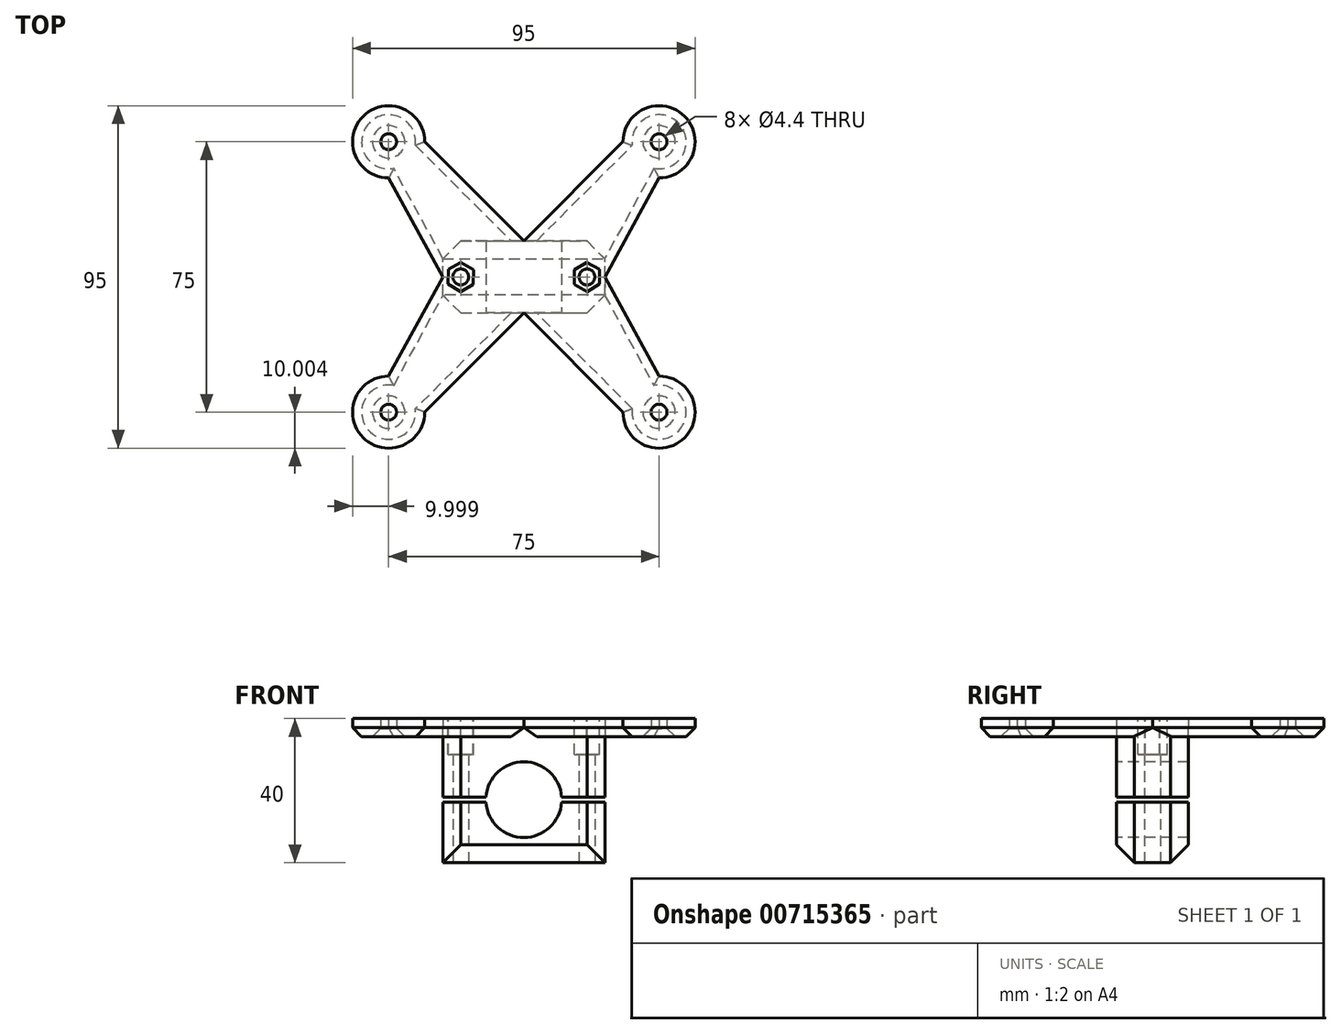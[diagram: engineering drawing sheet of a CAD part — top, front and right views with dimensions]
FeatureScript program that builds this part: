
annotation { "Feature Type Name" : "Feature", "Feature Type Description" : "" }
export const myFeature = defineFeature(function(context is Context, id is Id, definition is map)
    precondition{}
    {
        {
            var Q0;
            Q0=qCreatedBy(makeId("Top.planeOp"),FACE);
            var sketch = newSketch(context, id + "F0", { "sketchPlane" : qUnion([Q0])});
            skLineSegment(sketch, "E0.bottom", {"start": v(-29.97, 5.83) * mm, "end": v(15.03, 5.83) * mm});
            skLineSegment(sketch, "E0.top", {"start": v(-29.97, -14.17) * mm, "end": v(15.03, -14.17) * mm});
            skLineSegment(sketch, "E0.left", {"start": v(-29.97, 5.83) * mm, "end": v(-29.97, -14.17) * mm});
            skLineSegment(sketch, "E0.right", {"start": v(15.03, 5.83) * mm, "end": v(15.03, -14.17) * mm});
            skSolve(sketch);
        }
        {
            var Q0;
            Q0 = qSketchRegion(id + "F0", true);
            extrude(context, id + "F1", {"entities" : qUnion([Q0]), "depth" : 35 * mm, "offsetDistance" : 25 * mm});
        }
        {
            var Q0;
            Q0=makeQuery(id+"F1.opExtrude","SWEPT_FACE",FACE,{"disambiguationData":[OSD([sQuery(id+"F0.wireOp",EDGE,"E0.top")])]});
            var sketch = newSketch(context, id + "F2", { "sketchPlane" : qUnion([Q0])});
            skLineSegment(sketch, "E1", {"start": v(-7.47, 35) * mm, "end": v(-7.47, 0) * mm, "construction": true});
            skCircle(sketch, "E2", {"center": v(-7.47, 17.5) * mm, "radius": 10.5 * mm});
            skSolve(sketch);
        }
        {
            var Q0;
            Q0=makeQuery(id+"F2.imprint","IMPRINT",FACE,{"disambiguationData":[TD([[makeQuery(id+"F2.imprint","IMPRINT",EDGE,{"derivedFrom":sQuery(id+"F2.wireOp",EDGE,"E2")}),1.0]])]});
            extrude(context, id + "F3", {"entities" : qUnion([Q0]), "operationType" : NewBodyOperationType.REMOVE, "endBound" : BoundingType.UP_TO_NEXT, "oppositeDirection" : true, "depth" : 25 * mm, "offsetDistance" : 25 * mm});
        }
        {
            var Q0;
            Q0=makeQuery(id+"F1.opExtrude","CAP_FACE",FACE,{"disambiguationData":[OSD([sQuery(id+"F0.wireOp",EDGE,"E0.bottom"),sQuery(id+"F0.wireOp",EDGE,"E0.top"),sQuery(id+"F0.wireOp",EDGE,"E0.left"),sQuery(id+"F0.wireOp",EDGE,"E0.right")])],"isStart":false});
            var sketch = newSketch(context, id + "F4", { "sketchPlane" : qUnion([Q0])});
            skLineSegment(sketch, "E3", {"start": v(-7.47, 5.83) * mm, "end": v(-7.47, -14.17) * mm, "construction": true});
            skLineSegment(sketch, "E4.bottom", {"start": v(30.03, 33.33) * mm, "end": v(-44.97, 33.33) * mm});
            skLineSegment(sketch, "E4.top", {"start": v(30.03, -41.67) * mm, "end": v(-44.97, -41.67) * mm});
            skLineSegment(sketch, "E4.left", {"start": v(30.03, 33.33) * mm, "end": v(30.03, -41.67) * mm});
            skLineSegment(sketch, "E4.right", {"start": v(-44.97, 33.33) * mm, "end": v(-44.97, -41.67) * mm});
            skPoint(sketch, "E4.middle", {"position": v(-7.47, -4.17) * mm});
            skCircle(sketch, "E5", {"center": v(-44.97, 33.33) * mm, "radius": 10 * mm});
            skCircle(sketch, "E6", {"center": v(30.03, 33.33) * mm, "radius": 10 * mm});
            skCircle(sketch, "E7", {"center": v(30.03, -41.67) * mm, "radius": 10 * mm});
            skCircle(sketch, "E8", {"center": v(-44.97, -41.67) * mm, "radius": 10 * mm});
            skLineSegment(sketch, "E9", {"start": v(-44.97, -31.67) * mm, "end": v(-29.97, -4.17) * mm});
            skLineSegment(sketch, "E10", {"start": v(-34.97, -41.67) * mm, "end": v(-7.47, -14.17) * mm});
            skLineSegment(sketch, "E11", {"start": v(-7.47, -14.17) * mm, "end": v(20.03, -41.67) * mm});
            skLineSegment(sketch, "E12", {"start": v(-29.97, -4.17) * mm, "end": v(-44.97, 23.33) * mm});
            skLineSegment(sketch, "E13", {"start": v(-34.97, 33.33) * mm, "end": v(-7.47, 5.83) * mm});
            skLineSegment(sketch, "E14", {"start": v(-7.47, 5.83) * mm, "end": v(20.03, 33.33) * mm});
            skLineSegment(sketch, "E15", {"start": v(15.03, -4.17) * mm, "end": v(30.03, 23.33) * mm});
            skLineSegment(sketch, "E16", {"start": v(15.03, -4.17) * mm, "end": v(30.03, -31.67) * mm});
            skSolve(sketch);
        }
        {
            var Q0;
            {var subQ0=sQuery(id+"F4.wireOp",EDGE,"E4.right");var subQ1=sQuery(id+"F4.wireOp",EDGE,"E4.bottom");var subQ2=makeQuery(id+"F4.imprint","INTERSECT",VERTEX,{"derivedFrom":[subQ1,subQ0]});Q0=makeQuery(id+"F4.imprint","IMPRINT",FACE,{"disambiguationData":[TD([[makeQuery(id+"F4.imprint","IMPRINT",EDGE,{"disambiguationData":[TD([[subQ2,1.0]])],"derivedFrom":subQ1}),1.0]])]});}
            var Q1;
            {var subQ0=sQuery(id+"F4.wireOp",EDGE,"E4.right");var subQ1=sQuery(id+"F4.wireOp",EDGE,"E4.bottom");var subQ2=makeQuery(id+"F4.imprint","INTERSECT",VERTEX,{"derivedFrom":[subQ1,subQ0]});Q1=makeQuery(id+"F4.imprint","IMPRINT",FACE,{"disambiguationData":[TD([[makeQuery(id+"F4.imprint","IMPRINT",EDGE,{"disambiguationData":[TD([[subQ2,1.0]])],"derivedFrom":subQ1}),-1.0]])]});}
            var Q2;
            {var subQ1=sQuery(id+"F4.wireOp",EDGE,"E12");Q2=makeQuery(id+"F4.imprint","IMPRINT",FACE,{"disambiguationData":[TD([[makeQuery(id+"F4.imprint","IMPRINT",EDGE,{"derivedFrom":subQ1}),-1.0]])]});}
            var Q3;
            {var subQ4=sQuery(id+"F4.wireOp",EDGE,"E9");Q3=makeQuery(id+"F4.imprint","IMPRINT",FACE,{"disambiguationData":[TD([[makeQuery(id+"F4.imprint","IMPRINT",EDGE,{"derivedFrom":subQ4}),-1.0]])]});}
            var Q4;
            {var subQ0=sQuery(id+"F4.wireOp",EDGE,"E4.right");var subQ1=sQuery(id+"F4.wireOp",EDGE,"E4.top");var subQ2=makeQuery(id+"F4.imprint","INTERSECT",VERTEX,{"derivedFrom":[subQ1,subQ0]});Q4=makeQuery(id+"F4.imprint","IMPRINT",FACE,{"disambiguationData":[TD([[makeQuery(id+"F4.imprint","IMPRINT",EDGE,{"disambiguationData":[TD([[subQ2,1.0]])],"derivedFrom":subQ1}),-1.0]])]});}
            var Q5;
            {var subQ0=sQuery(id+"F4.wireOp",EDGE,"E4.right");var subQ1=sQuery(id+"F4.wireOp",EDGE,"E4.top");var subQ2=makeQuery(id+"F4.imprint","INTERSECT",VERTEX,{"derivedFrom":[subQ1,subQ0]});Q5=makeQuery(id+"F4.imprint","IMPRINT",FACE,{"disambiguationData":[TD([[makeQuery(id+"F4.imprint","IMPRINT",EDGE,{"disambiguationData":[TD([[subQ2,1.0]])],"derivedFrom":subQ1}),1.0]])]});}
            var Q6;
            {var subQ4=makeQuery(id+"F1.opExtrude","CAP_EDGE",EDGE,{"disambiguationData":[OSD([sQuery(id+"F0.wireOp",EDGE,"E0.left")])],"isStart":false});var subQ6=makeQuery(id+"F1.opExtrude","CAP_EDGE",EDGE,{"disambiguationData":[OSD([sQuery(id+"F0.wireOp",EDGE,"E0.bottom")])],"isStart":false});var subQ9=makeQuery(id+"F4.imprint","INTERSECT",VERTEX,{"derivedFrom":[subQ6,subQ4]});Q6=makeQuery(id+"F4.imprint","IMPRINT",FACE,{"disambiguationData":[TD([[makeQuery(id+"F4.imprint","IMPRINT",EDGE,{"disambiguationData":[TD([[subQ9,-1.0]])],"derivedFrom":subQ6}),-1.0]])]});}
            var Q7;
            {var subQ1=sQuery(id+"F4.wireOp",EDGE,"E14");Q7=makeQuery(id+"F4.imprint","IMPRINT",FACE,{"disambiguationData":[TD([[makeQuery(id+"F4.imprint","IMPRINT",EDGE,{"derivedFrom":subQ1}),-1.0]])]});}
            var Q8;
            {var subQ0=sQuery(id+"F4.wireOp",EDGE,"E4.left");var subQ1=sQuery(id+"F4.wireOp",EDGE,"E4.bottom");var subQ2=makeQuery(id+"F4.imprint","INTERSECT",VERTEX,{"derivedFrom":[subQ1,subQ0]});Q8=makeQuery(id+"F4.imprint","IMPRINT",FACE,{"disambiguationData":[TD([[makeQuery(id+"F4.imprint","IMPRINT",EDGE,{"disambiguationData":[TD([[subQ2,-1.0]])],"derivedFrom":subQ1}),1.0]])]});}
            var Q9;
            {var subQ0=sQuery(id+"F4.wireOp",EDGE,"E4.left");var subQ1=sQuery(id+"F4.wireOp",EDGE,"E4.bottom");var subQ2=makeQuery(id+"F4.imprint","INTERSECT",VERTEX,{"derivedFrom":[subQ1,subQ0]});Q9=makeQuery(id+"F4.imprint","IMPRINT",FACE,{"disambiguationData":[TD([[makeQuery(id+"F4.imprint","IMPRINT",EDGE,{"disambiguationData":[TD([[subQ2,-1.0]])],"derivedFrom":subQ1}),-1.0]])]});}
            var Q10;
            {var subQ1=sQuery(id+"F4.wireOp",EDGE,"E11");Q10=makeQuery(id+"F4.imprint","IMPRINT",FACE,{"disambiguationData":[TD([[makeQuery(id+"F4.imprint","IMPRINT",EDGE,{"derivedFrom":subQ1}),1.0]])]});}
            var Q11;
            {var subQ0=sQuery(id+"F4.wireOp",EDGE,"E4.left");var subQ1=sQuery(id+"F4.wireOp",EDGE,"E4.top");var subQ2=makeQuery(id+"F4.imprint","INTERSECT",VERTEX,{"derivedFrom":[subQ1,subQ0]});Q11=makeQuery(id+"F4.imprint","IMPRINT",FACE,{"disambiguationData":[TD([[makeQuery(id+"F4.imprint","IMPRINT",EDGE,{"disambiguationData":[TD([[subQ2,-1.0]])],"derivedFrom":subQ1}),-1.0]])]});}
            var Q12;
            {var subQ0=sQuery(id+"F4.wireOp",EDGE,"E4.left");var subQ1=sQuery(id+"F4.wireOp",EDGE,"E4.top");var subQ2=makeQuery(id+"F4.imprint","INTERSECT",VERTEX,{"derivedFrom":[subQ1,subQ0]});Q12=makeQuery(id+"F4.imprint","IMPRINT",FACE,{"disambiguationData":[TD([[makeQuery(id+"F4.imprint","IMPRINT",EDGE,{"disambiguationData":[TD([[subQ2,-1.0]])],"derivedFrom":subQ1}),1.0]])]});}
            extrude(context, id + "F5", {"entities" : qUnion([Q0, Q1, Q2, Q3, Q4, Q5, Q6, Q7, Q8, Q9, Q10, Q11, Q12]), "operationType" : NewBodyOperationType.ADD, "depth" : 5 * mm, "offsetDistance" : 25 * mm});
        }
        {
            var Q0;
            Q0=sQuery(id+"F4.wireOp",VERTEX,"E4.right.end");
            var Q1;
            Q1=sQuery(id+"F4.wireOp",VERTEX,"E4.left.end");
            var Q2;
            Q2=sQuery(id+"F4.wireOp",VERTEX,"E6.center");
            var Q3;
            Q3=sQuery(id+"F4.wireOp",VERTEX,"E4.right.start");
            var Q4;
            Q4=makeQuery(id+"F1.opExtrude","SWEPT_BODY",BODY,{"disambiguationData":[OSD([sQuery(id+"F0.wireOp",EDGE,"E0.bottom"),sQuery(id+"F0.wireOp",EDGE,"E0.top"),sQuery(id+"F0.wireOp",EDGE,"E0.left"),sQuery(id+"F0.wireOp",EDGE,"E0.right")])]});
            hole(context, id + "F6", {"style" : HoleStyle.C_SINK, "endStyle" : HoleEndStyle.BLIND, "oppositeDirection" : true, "standardTappedOrClearance" : lookupTablePath({ "standard" : "ISO", "fit" : "Normal", "size" : "M4", "type" : "Clearance" }), "standardBlindInLast" : lookupTablePath({ "fit" : "Standard", "standard" : "ISO", "size" : "M4", "type" : "Clearance" }), "holeDiameter" : 4.4 * mm, "cSinkDiameter" : 8.96 * mm, "cSinkAngle" : 90 * degree, "majorDiameter" : 5 * mm, "holeDepth" : 35 * mm, "isTappedThrough" : true, "tappedDepth" : 12 * mm, "tapClearance" : 3, "locations" : qUnion([Q0, Q1, Q2, Q3]), "scope" : qUnion([Q4])});
        }
        {
            var Q0;
            Q0=makeQuery(id+"F1.opExtrude","CAP_FACE",FACE,{"disambiguationData":[OSD([sQuery(id+"F0.wireOp",EDGE,"E0.bottom"),sQuery(id+"F0.wireOp",EDGE,"E0.top"),sQuery(id+"F0.wireOp",EDGE,"E0.left"),sQuery(id+"F0.wireOp",EDGE,"E0.right")])],"isStart":true});
            var sketch = newSketch(context, id + "F7", { "sketchPlane" : qUnion([Q0])});
            skLineSegment(sketch, "E17", {"start": v(-29.97, 4.17) * mm, "end": v(-24.97, 4.17) * mm, "construction": true});
            skLineSegment(sketch, "E18.MirrorCS", {"start": v(15.03, 4.17) * mm, "end": v(10.03, 4.17) * mm, "construction": true});
            skSolve(sketch);
        }
        {
            var Q0;
            Q0=sQuery(id+"F7.wireOp",VERTEX,"E17.end");
            var Q1;
            Q1=sQuery(id+"F7.wireOp",VERTEX,"E18.MirrorCS.end");
            var Q2;
            Q2=makeQuery(id+"F1.opExtrude","SWEPT_BODY",BODY,{"disambiguationData":[OSD([sQuery(id+"F0.wireOp",EDGE,"E0.bottom"),sQuery(id+"F0.wireOp",EDGE,"E0.top"),sQuery(id+"F0.wireOp",EDGE,"E0.left"),sQuery(id+"F0.wireOp",EDGE,"E0.right")])]});
            hole(context, id + "F8", {"style" : HoleStyle.SIMPLE, "endStyle" : HoleEndStyle.THROUGH, "standardTappedOrClearance" : lookupTablePath({ "standard" : "ISO", "fit" : "Normal", "size" : "M4", "type" : "Clearance" }), "standardBlindInLast" : lookupTablePath({ "fit" : "Standard", "standard" : "ISO", "size" : "M4", "type" : "Clearance" }), "holeDiameter" : 4.4 * mm, "majorDiameter" : 5 * mm, "isTappedThrough" : true, "tappedDepth" : 12 * mm, "tapClearance" : 3, "locations" : qUnion([Q0, Q1]), "scope" : qUnion([Q2])});
        }
        {
            var Q0;
            Q0=makeQuery(id+"F5.opExtrude","CAP_FACE",FACE,{"disambiguationData":[OSD([sQuery(id+"F4.wireOp",EDGE,"E5"),sQuery(id+"F4.wireOp",EDGE,"E6"),sQuery(id+"F4.wireOp",EDGE,"E7"),sQuery(id+"F4.wireOp",EDGE,"E8"),sQuery(id+"F4.wireOp",EDGE,"E9"),sQuery(id+"F4.wireOp",EDGE,"E10"),sQuery(id+"F4.wireOp",EDGE,"E11"),sQuery(id+"F4.wireOp",EDGE,"E12"),sQuery(id+"F4.wireOp",EDGE,"E13"),sQuery(id+"F4.wireOp",EDGE,"E14"),sQuery(id+"F4.wireOp",EDGE,"E15"),sQuery(id+"F4.wireOp",EDGE,"E16")])],"isStart":false});
            var sketch = newSketch(context, id + "F9", { "sketchPlane" : qUnion([Q0])});
            skCircle(sketch, "E19.cCircle", {"center": v(10.03, -4.17) * mm, "radius": 3.5 * mm, "construction": true});
            skLineSegment(sketch, "E19.0", {"start": v(9.97, -0.12) * mm, "end": v(13.5, -2.1) * mm});
            skLineSegment(sketch, "E19.1", {"start": v(13.5, -2.1) * mm, "end": v(13.56, -6.14) * mm});
            skLineSegment(sketch, "E19.2", {"start": v(13.56, -6.14) * mm, "end": v(10.09, -8.2) * mm});
            skLineSegment(sketch, "E19.3", {"start": v(10.09, -8.2) * mm, "end": v(6.56, -6.24) * mm});
            skLineSegment(sketch, "E19.4", {"start": v(6.56, -6.24) * mm, "end": v(6.5, -2.2) * mm});
            skLineSegment(sketch, "E19.5", {"start": v(6.5, -2.2) * mm, "end": v(9.97, -0.12) * mm});
            skPoint(sketch, "E19.0.midPoint", {"position": v(11.74, -1.1) * mm});
            skLineSegment(sketch, "E20.MirrorCS", {"start": v(-21.44, -2.2) * mm, "end": v(-24.91, -0.12) * mm});
            skLineSegment(sketch, "E21.MirrorCS", {"start": v(-21.5, -6.24) * mm, "end": v(-21.44, -2.2) * mm});
            skLineSegment(sketch, "E22.MirrorCS", {"start": v(-25.03, -8.2) * mm, "end": v(-21.5, -6.24) * mm});
            skLineSegment(sketch, "E23.MirrorCS", {"start": v(-28.5, -6.14) * mm, "end": v(-25.03, -8.2) * mm});
            skLineSegment(sketch, "E24.MirrorCS", {"start": v(-28.44, -2.1) * mm, "end": v(-28.5, -6.14) * mm});
            skLineSegment(sketch, "E25.MirrorCS", {"start": v(-24.91, -0.12) * mm, "end": v(-28.44, -2.1) * mm});
            skSolve(sketch);
        }
        {
            var Q0;
            Q0=makeQuery(id+"F9.imprint","IMPRINT",FACE,{"disambiguationData":[TD([[makeQuery(id+"F9.imprint","IMPRINT",EDGE,{"derivedFrom":sQuery(id+"F9.wireOp",EDGE,"E20.MirrorCS")}),1.0]])]});
            var Q1;
            Q1=makeQuery(id+"F9.imprint","IMPRINT",FACE,{"disambiguationData":[TD([[makeQuery(id+"F9.imprint","IMPRINT",EDGE,{"derivedFrom":sQuery(id+"F9.wireOp",EDGE,"E19.0")}),-1.0]])]});
            extrude(context, id + "F10", {"entities" : qUnion([Q0, Q1]), "operationType" : NewBodyOperationType.REMOVE, "oppositeDirection" : true, "depth" : 10 * mm, "offsetDistance" : 25 * mm});
        }
        {
            var Q0;
            Q0=makeQuery(id+"F5.opExtrude","CAP_EDGE",EDGE,{"disambiguationData":[OSD([sQuery(id+"F4.wireOp",EDGE,"E11")])],"isStart":true});
            var Q1;
            Q1=makeQuery(id+"F5.opExtrude","CAP_EDGE",EDGE,{"disambiguationData":[OSD([sQuery(id+"F4.wireOp",EDGE,"E7")])],"isStart":true});
            var Q2;
            Q2=makeQuery(id+"F5.opExtrude","CAP_EDGE",EDGE,{"disambiguationData":[OSD([sQuery(id+"F4.wireOp",EDGE,"E16")])],"isStart":true});
            chamfer(context, id + "F11", {"entities" : qUnion([Q0, Q1, Q2]), "width" : 2.5 * mm, "tangentPropagation" : true});
        }
        {
            var Q0;
            Q0=makeQuery(id+"F5.opExtrude","CAP_EDGE",EDGE,{"disambiguationData":[OSD([sQuery(id+"F4.wireOp",EDGE,"E15")])],"isStart":true});
            var Q1;
            Q1=makeQuery(id+"F5.opExtrude","CAP_EDGE",EDGE,{"disambiguationData":[OSD([sQuery(id+"F4.wireOp",EDGE,"E6")])],"isStart":true});
            var Q2;
            Q2=makeQuery(id+"F5.opExtrude","CAP_EDGE",EDGE,{"disambiguationData":[OSD([sQuery(id+"F4.wireOp",EDGE,"E14")])],"isStart":true});
            chamfer(context, id + "F12", {"entities" : qUnion([Q0, Q1, Q2]), "width" : 2.5 * mm, "tangentPropagation" : true});
        }
        {
            var Q0;
            Q0=makeQuery(id+"F5.opExtrude","CAP_EDGE",EDGE,{"disambiguationData":[OSD([sQuery(id+"F4.wireOp",EDGE,"E10")])],"isStart":true});
            var Q1;
            Q1=makeQuery(id+"F5.opExtrude","CAP_EDGE",EDGE,{"disambiguationData":[OSD([sQuery(id+"F4.wireOp",EDGE,"E8")])],"isStart":true});
            var Q2;
            Q2=makeQuery(id+"F5.opExtrude","CAP_EDGE",EDGE,{"disambiguationData":[OSD([sQuery(id+"F4.wireOp",EDGE,"E9")])],"isStart":true});
            chamfer(context, id + "F13", {"entities" : qUnion([Q0, Q1, Q2]), "width" : 2.5 * mm, "tangentPropagation" : true});
        }
        {
            var Q0;
            Q0=makeQuery(id+"F5.opExtrude","CAP_EDGE",EDGE,{"disambiguationData":[OSD([sQuery(id+"F4.wireOp",EDGE,"E12")])],"isStart":true});
            var Q1;
            Q1=makeQuery(id+"F5.opExtrude","CAP_EDGE",EDGE,{"disambiguationData":[OSD([sQuery(id+"F4.wireOp",EDGE,"E13")])],"isStart":true});
            var Q2;
            Q2=makeQuery(id+"F5.opExtrude","CAP_EDGE",EDGE,{"disambiguationData":[OSD([sQuery(id+"F4.wireOp",EDGE,"E5")])],"isStart":true});
            chamfer(context, id + "F14", {"entities" : qUnion([Q0, Q1, Q2]), "width" : 2.5 * mm, "tangentPropagation" : true});
        }
        {
            var Q0;
            Q0=makeQuery(id+"F1.opExtrude","SWEPT_EDGE",EDGE,{"disambiguationData":[OSD([sQuery(id+"F0.wireOp",EDGE,"E0.top"),sQuery(id+"F0.wireOp",EDGE,"E0.right")])]});
            var Q1;
            Q1=makeQuery(id+"F1.opExtrude","SWEPT_EDGE",EDGE,{"disambiguationData":[OSD([sQuery(id+"F0.wireOp",EDGE,"E0.bottom"),sQuery(id+"F0.wireOp",EDGE,"E0.right")])]});
            var Q2;
            Q2=makeQuery(id+"F1.opExtrude","SWEPT_EDGE",EDGE,{"disambiguationData":[OSD([sQuery(id+"F0.wireOp",EDGE,"E0.top"),sQuery(id+"F0.wireOp",EDGE,"E0.left")])]});
            var Q3;
            Q3=makeQuery(id+"F1.opExtrude","SWEPT_EDGE",EDGE,{"disambiguationData":[OSD([sQuery(id+"F0.wireOp",EDGE,"E0.bottom"),sQuery(id+"F0.wireOp",EDGE,"E0.left")])]});
            var Q4;
            Q4=makeQuery(id+"F1.opExtrude","CAP_EDGE",EDGE,{"disambiguationData":[OSD([sQuery(id+"F0.wireOp",EDGE,"E0.bottom")])],"isStart":true});
            var Q5;
            Q5=makeQuery(id+"F1.opExtrude","CAP_EDGE",EDGE,{"disambiguationData":[OSD([sQuery(id+"F0.wireOp",EDGE,"E0.top")])],"isStart":true});
            chamfer(context, id + "F15", {"entities" : qUnion([Q0, Q1, Q2, Q3, Q4, Q5]), "width" : 5 * mm, "tangentPropagation" : true});
        }
        {
            var Q0;
            Q0=makeQuery(id+"F1.opExtrude","SWEPT_FACE",FACE,{"disambiguationData":[OSD([sQuery(id+"F0.wireOp",EDGE,"E0.top")])]});
            var sketch = newSketch(context, id + "F16", { "sketchPlane" : qUnion([Q0])});
            skLineSegment(sketch, "E26.bottom", {"start": v(-35.85, 16.75) * mm, "end": v(20.9, 16.75) * mm});
            skLineSegment(sketch, "E26.top", {"start": v(-35.85, 18.25) * mm, "end": v(20.9, 18.25) * mm});
            skLineSegment(sketch, "E26.left", {"start": v(-35.85, 16.75) * mm, "end": v(-35.85, 18.25) * mm});
            skLineSegment(sketch, "E26.right", {"start": v(20.9, 16.75) * mm, "end": v(20.9, 18.25) * mm});
            skPoint(sketch, "E26.middle", {"position": v(-7.47, 17.5) * mm});
            skSolve(sketch);
        }
        {
            var Q0;
            Q0 = qSketchRegion(id + "F16", true);
            extrude(context, id + "F17", {"entities" : qUnion([Q0]), "operationType" : NewBodyOperationType.REMOVE, "oppositeDirection" : true, "depth" : 25 * mm, "offsetDistance" : 25 * mm});
        }
    });
